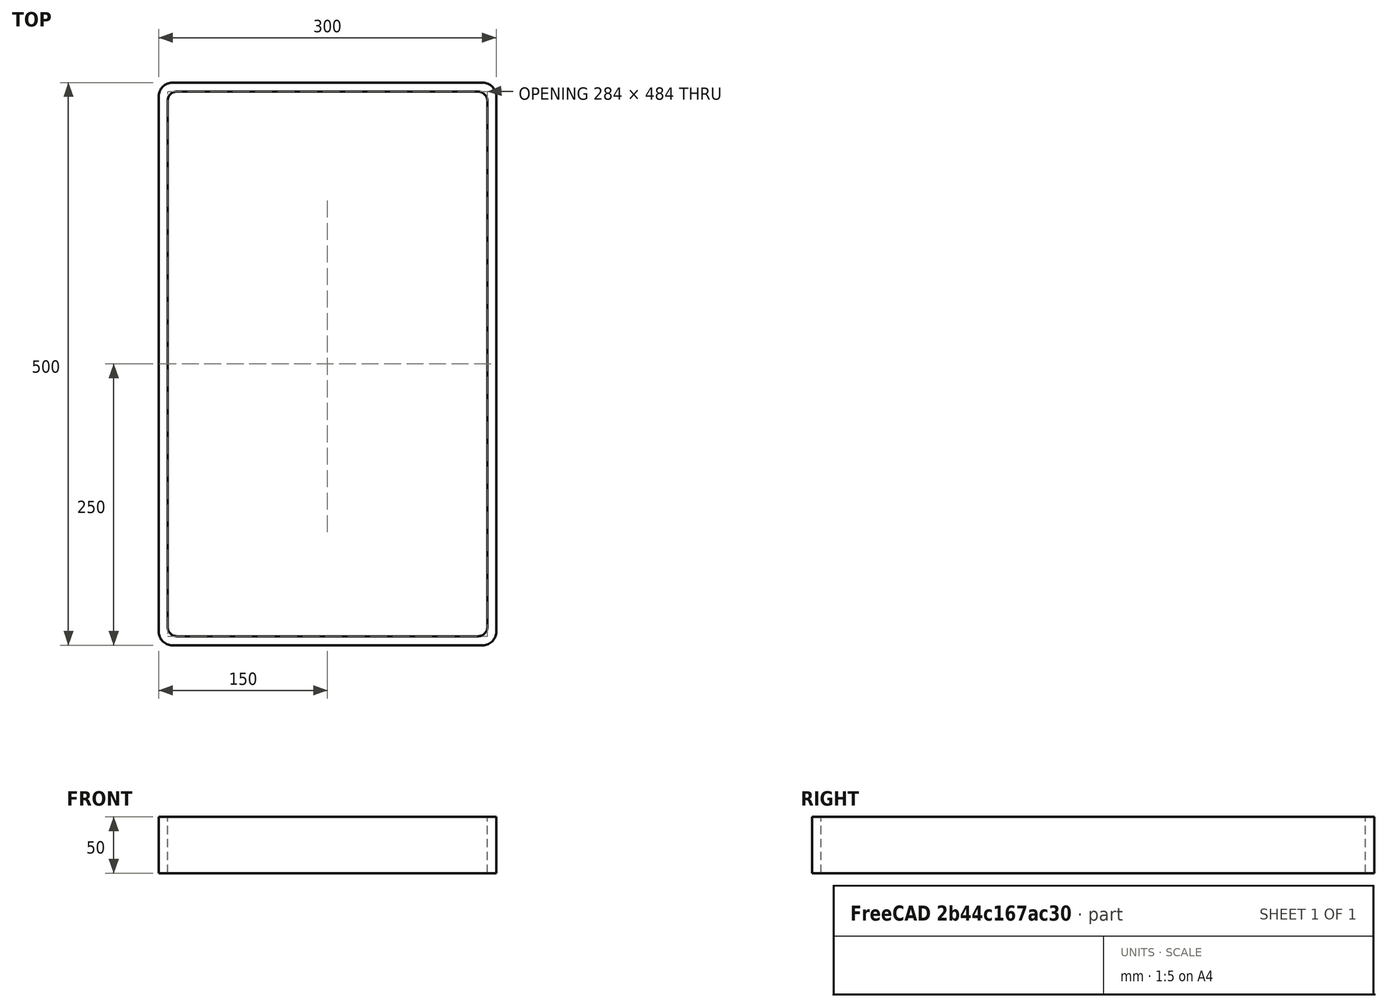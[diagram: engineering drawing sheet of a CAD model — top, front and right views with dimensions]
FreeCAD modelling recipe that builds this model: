
FCSTD DOCUMENT  (FreeCAD 0.15R4671 (Git))
Label: Rectangular hollow section 500x300x8 EN10219 S235JRH
License: All rights reserved
LicenseURL: http://en.wikipedia.org/wiki/All_rights_reserved
objects: Sketcher::SketchObject×1, Part::Extrusion×1
note: 2 computed .brp shape members not serialized (recipe doc carries the construction recipe); baked Part::Feature solids carry a one-line shape summary decoded from their .brp

FEATURE [Sketcher::SketchObject] Sketch
  sketch-geometry (16):
    g0: LineSegment StartX=-134 StartY=242 StartZ=0 EndX=134 EndY=242 EndZ=0
    g1: LineSegment StartX=142 StartY=234 StartZ=0 EndX=142 EndY=-234 EndZ=0
    g2: LineSegment StartX=134 StartY=-242 StartZ=0 EndX=-134 EndY=-242 EndZ=0
    g3: LineSegment StartX=-142 StartY=-234 StartZ=0 EndX=-142 EndY=234 EndZ=0
    g4: LineSegment StartX=-138 StartY=250 StartZ=0 EndX=138 EndY=250 EndZ=0
    g5: LineSegment StartX=150 StartY=238 StartZ=0 EndX=150 EndY=-238 EndZ=0
    g6: LineSegment StartX=138 StartY=-250 StartZ=0 EndX=-138 EndY=-250 EndZ=0
    g7: LineSegment StartX=-150 StartY=-238 StartZ=0 EndX=-150 EndY=238 EndZ=0
    g8: ArcOfCircle CenterX=-134 CenterY=234 CenterZ=0 NormalX=0 NormalY=0 NormalZ=1 Radius=8 StartAngle=1.5708 EndAngle=3.14159
    g9: ArcOfCircle CenterX=134 CenterY=234 CenterZ=0 NormalX=0 NormalY=0 NormalZ=1 Radius=8 StartAngle=0 EndAngle=1.5708
    g10: ArcOfCircle CenterX=134 CenterY=-234 CenterZ=0 NormalX=0 NormalY=0 NormalZ=1 Radius=8 StartAngle=4.71239 EndAngle=6.28319
    g11: ArcOfCircle CenterX=-134 CenterY=-234 CenterZ=0 NormalX=0 NormalY=0 NormalZ=1 Radius=8 StartAngle=3.14159 EndAngle=4.71239
    g12: ArcOfCircle CenterX=138 CenterY=238 CenterZ=0 NormalX=0 NormalY=0 NormalZ=1 Radius=12 StartAngle=0 EndAngle=1.5708
    g13: ArcOfCircle CenterX=138 CenterY=-238 CenterZ=0 NormalX=0 NormalY=0 NormalZ=1 Radius=12 StartAngle=4.71239 EndAngle=6.28319
    g14: ArcOfCircle CenterX=-138 CenterY=-238 CenterZ=0 NormalX=0 NormalY=0 NormalZ=1 Radius=12 StartAngle=3.14159 EndAngle=4.71239
    g15: ArcOfCircle CenterX=-138 CenterY=238 CenterZ=0 NormalX=0 NormalY=0 NormalZ=1 Radius=12 StartAngle=1.5708 EndAngle=3.14159
  constraints (36):
    c: Horizontal(g2)
    c: Vertical(g3)
    c: Horizontal(g6)
    c: Vertical(g7)
    c: Tangent(g3,g8) = 1.5708
    c: Tangent(g0,g8) = 1.5708
    c: Tangent(g0,g9) = 1.5708
    c: Tangent(g1,g9) = 1.5708
    c: Tangent(g1,g10) = 1.5708
    c: Tangent(g2,g10) = 1.5708
    c: Tangent(g2,g11) = 1.5708
    c: Tangent(g3,g11) = 1.5708
    c: Tangent(g4,g12) = 1.5708
    c: Tangent(g5,g12) = 1.5708
    c: Tangent(g5,g13) = 1.5708
    c: Tangent(g6,g13) = 1.5708
    c: Tangent(g6,g14) = 1.5708
    c: Tangent(g7,g14) = 1.5708
    c: Tangent(g7,g15) = 1.5708
    c: Tangent(g4,g15) = 1.5708
    c: Equal(g9,g8)
    c: Equal(g9,g11)
    c: Equal(g9,g10)
    c: Equal(g12,g15)
    c: Equal(g12,g14)
    c: Equal(g12,g13)
    c: Symmetric(g4,g6,g-1)
    c: Symmetric(g7,g5,g-2)
    c: DistanceY(g4,g6) = -500
    c: DistanceX(g7,g5) = 300
    c: Symmetric(g3,g1,g-2)
    c: Symmetric(g0,g2,g-1)
    c: DistanceY(g0,g4) = 8
    c: DistanceX(g5,g1) = -8
    c: Radius(g9) = 8
    c: Radius(g12) = 12
FEATURE [Part::Extrusion] Extrude  label="Rectangular hollow section 500x300x8 EN10219 S235JRH"
  Base = -> Sketch
  Dir = (0,0,50)
  Solid = true
